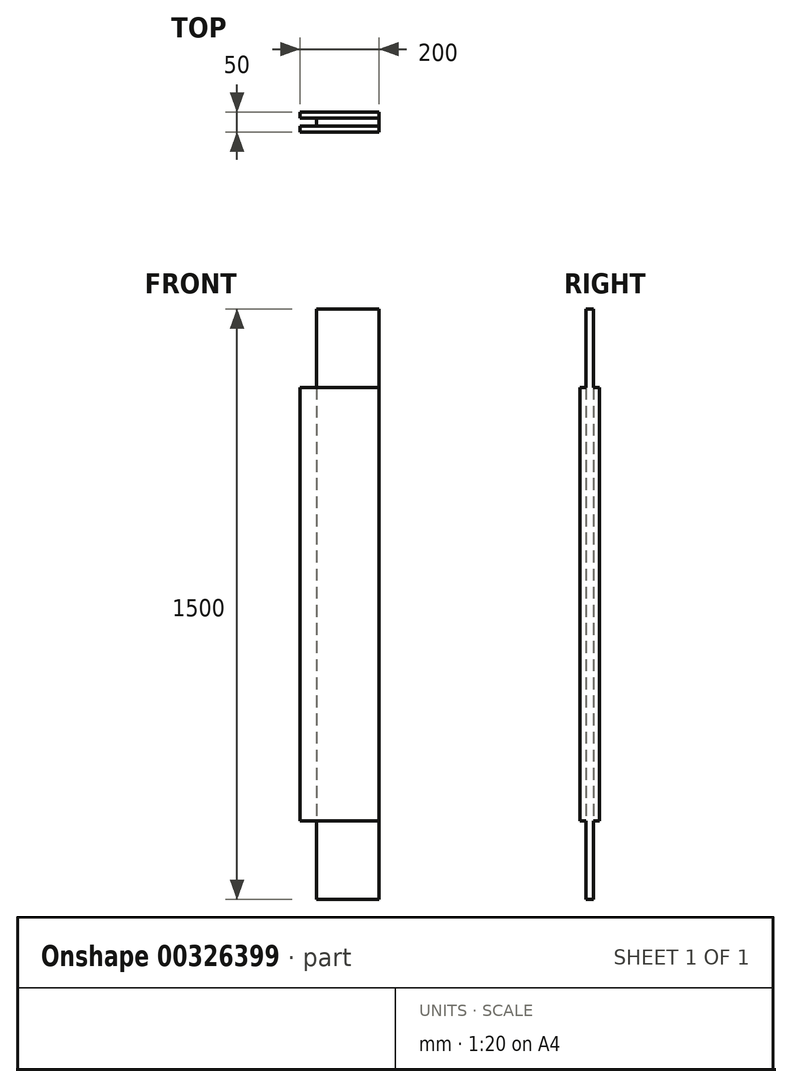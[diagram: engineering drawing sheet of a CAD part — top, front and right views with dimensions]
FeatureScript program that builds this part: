
annotation { "Feature Type Name" : "Feature", "Feature Type Description" : "" }
export const myFeature = defineFeature(function(context is Context, id is Id, definition is map)
    precondition{}
    {
        {
            var Q0;
            Q0=qCreatedBy(makeId("Top.planeOp"),FACE);
            var sketch = newSketch(context, id + "F0", { "sketchPlane" : qUnion([Q0])});
            skLineSegment(sketch, "E0.bottom", {"start": v(0, 0) * mm, "end": v(0, 0) * mm});
            skLineSegment(sketch, "E0.top", {"start": v(0, -16.02) * mm, "end": v(0, -16.02) * mm});
            skLineSegment(sketch, "E0.left", {"start": v(0, 0) * mm, "end": v(0, -16.02) * mm});
            skLineSegment(sketch, "E0.right", {"start": v(0, 0) * mm, "end": v(0, -16.02) * mm});
            skPoint(sketch, "E0.middle", {"position": v(0, -8) * mm});
            skLineSegment(sketch, "E1.bottom", {"start": v(-100, 25) * mm, "end": v(100, 25) * mm});
            skLineSegment(sketch, "E1.top", {"start": v(-100, -25) * mm, "end": v(100, -25) * mm});
            skLineSegment(sketch, "E1.left", {"start": v(-100, 25) * mm, "end": v(-100, -25) * mm});
            skLineSegment(sketch, "E1.right", {"start": v(100, 25) * mm, "end": v(100, -25) * mm});
            skPoint(sketch, "E1.middle", {"position": v(0, 0) * mm});
            skSolve(sketch);
        }
        {
            var Q0;
            Q0=makeQuery(id+"F0.imprint","IMPRINT",FACE,{"disambiguationData":[TD([[makeQuery(id+"F0.imprint","IMPRINT",EDGE,{"derivedFrom":sQuery(id+"F0.wireOp",EDGE,"E1.bottom")}),-1.0]])]});
            extrude(context, id + "F1", {"entities" : qUnion([Q0]), "endBound" : BoundingType.SYMMETRIC, "depth" : 1500 * mm});
        }
        {
            var Q0;
            Q0=makeQuery(id+"F1.opExtrude","CAP_FACE",FACE,{"disambiguationData":[OSD([sQuery(id+"F0.wireOp",EDGE,"E1.bottom"),sQuery(id+"F0.wireOp",EDGE,"E1.top"),sQuery(id+"F0.wireOp",EDGE,"E1.left"),sQuery(id+"F0.wireOp",EDGE,"E1.right")])],"isStart":true});
            var sketch = newSketch(context, id + "F2", { "sketchPlane" : qUnion([Q0])});
            skLineSegment(sketch, "E2.bottom", {"start": v(100, 25) * mm, "end": v(60, 25) * mm});
            skLineSegment(sketch, "E2.top", {"start": v(100, 10) * mm, "end": v(60, 10) * mm});
            skLineSegment(sketch, "E2.left", {"start": v(100, 25) * mm, "end": v(100, 10) * mm});
            skLineSegment(sketch, "E2.right", {"start": v(60, 25) * mm, "end": v(60, 10) * mm});
            skLineSegment(sketch, "E3.MirrorCS", {"start": v(60, -25) * mm, "end": v(60, -10) * mm});
            skLineSegment(sketch, "E4.MirrorCS", {"start": v(100, -25) * mm, "end": v(100, -10) * mm});
            skLineSegment(sketch, "E5.MirrorCS", {"start": v(100, -25) * mm, "end": v(60, -25) * mm});
            skLineSegment(sketch, "E6.MirrorCS", {"start": v(100, -10) * mm, "end": v(60, -10) * mm});
            skLineSegment(sketch, "E7.bottom", {"start": v(-100, -10) * mm, "end": v(-58, -10) * mm});
            skLineSegment(sketch, "E7.top", {"start": v(-100, 10) * mm, "end": v(-58, 10) * mm});
            skLineSegment(sketch, "E7.left", {"start": v(-100, -10) * mm, "end": v(-100, 10) * mm});
            skLineSegment(sketch, "E7.right", {"start": v(-58, -10) * mm, "end": v(-58, 10) * mm});
            skSolve(sketch);
        }
        {
            var Q0;
            Q0=makeQuery(id+"F2.imprint","IMPRINT",FACE,{"disambiguationData":[TD([[makeQuery(id+"F2.imprint","IMPRINT",EDGE,{"derivedFrom":sQuery(id+"F2.wireOp",EDGE,"E7.bottom")}),1.0]])]});
            var Q1;
            Q1=makeQuery(id+"F1.opExtrude","CAP_FACE",FACE,{"disambiguationData":[OSD([sQuery(id+"F0.wireOp",EDGE,"E1.bottom"),sQuery(id+"F0.wireOp",EDGE,"E1.top"),sQuery(id+"F0.wireOp",EDGE,"E1.left"),sQuery(id+"F0.wireOp",EDGE,"E1.right")])],"isStart":true});
            extrude(context, id + "F3", {"entities" : qUnion([Q0]), "operationType" : NewBodyOperationType.REMOVE, "endBound" : BoundingType.UP_TO_NEXT, "oppositeDirection" : true, "endBoundEntityFace" : qUnion([Q1]), "depth" : 25 * mm});
        }
        {
            var Q0;
            {var subQ1=sQuery(id+"F0.wireOp",EDGE,"E1.left");var subQ2=sQuery(id+"F0.wireOp",EDGE,"E1.top");Q0=makeQuery(id+"F3.boolean.opBoolean","SPLIT",FACE,{"disambiguationData":[TD([makeQuery(id+"F1.opExtrude","SWEPT_FACE",FACE,{"disambiguationData":[OSD([subQ2])]})])],"derivedFrom":makeQuery(id+"F1.opExtrude","SWEPT_FACE",FACE,{"disambiguationData":[OSD([subQ1])]})});}
            var sketch = newSketch(context, id + "F4", { "sketchPlane" : qUnion([Q0])});
            skLineSegment(sketch, "E8.bottom", {"start": v(25, -750) * mm, "end": v(10, -750) * mm});
            skLineSegment(sketch, "E8.top", {"start": v(25, -550) * mm, "end": v(10, -550) * mm});
            skLineSegment(sketch, "E8.left", {"start": v(25, -750) * mm, "end": v(25, -550) * mm});
            skLineSegment(sketch, "E8.right", {"start": v(10, -750) * mm, "end": v(10, -550) * mm});
            skLineSegment(sketch, "E9.MirrorCS", {"start": v(25, 750) * mm, "end": v(10, 750) * mm});
            skLineSegment(sketch, "E10.MirrorCS", {"start": v(25, 550) * mm, "end": v(10, 550) * mm});
            skLineSegment(sketch, "E11.MirrorCS", {"start": v(10, 750) * mm, "end": v(10, 550) * mm});
            skLineSegment(sketch, "E12.MirrorCS", {"start": v(25, 750) * mm, "end": v(25, 550) * mm});
            skLineSegment(sketch, "E13.MirrorCS", {"start": v(-25, -750) * mm, "end": v(-10, -750) * mm});
            skLineSegment(sketch, "E14.MirrorCS", {"start": v(-25, -550) * mm, "end": v(-10, -550) * mm});
            skLineSegment(sketch, "E15.MirrorCS", {"start": v(-25, -750) * mm, "end": v(-25, -550) * mm});
            skLineSegment(sketch, "E16.MirrorCS", {"start": v(-10, -750) * mm, "end": v(-10, -550) * mm});
            skLineSegment(sketch, "E17.MirrorCS", {"start": v(-25, 550) * mm, "end": v(-10, 550) * mm});
            skLineSegment(sketch, "E18.MirrorCS", {"start": v(-25, 750) * mm, "end": v(-10, 750) * mm});
            skLineSegment(sketch, "E19.MirrorCS", {"start": v(-25, 750) * mm, "end": v(-25, 550) * mm});
            skLineSegment(sketch, "E20.MirrorCS", {"start": v(-10, 750) * mm, "end": v(-10, 550) * mm});
            skSolve(sketch);
        }
        {
            var Q0;
            Q0=makeQuery(id+"F4.imprint","IMPRINT",FACE,{"disambiguationData":[TD([[makeQuery(id+"F4.imprint","IMPRINT",EDGE,{"derivedFrom":sQuery(id+"F4.wireOp",EDGE,"E17.MirrorCS")}),1.0]])]});
            var Q1;
            Q1=makeQuery(id+"F4.imprint","IMPRINT",FACE,{"disambiguationData":[TD([[makeQuery(id+"F4.imprint","IMPRINT",EDGE,{"derivedFrom":sQuery(id+"F4.wireOp",EDGE,"E11.MirrorCS")}),1.0]])]});
            var Q2;
            Q2=makeQuery(id+"F4.imprint","IMPRINT",FACE,{"disambiguationData":[TD([[makeQuery(id+"F4.imprint","IMPRINT",EDGE,{"derivedFrom":sQuery(id+"F4.wireOp",EDGE,"E8.bottom")}),1.0]])]});
            var Q3;
            Q3=makeQuery(id+"F4.imprint","IMPRINT",FACE,{"disambiguationData":[TD([[makeQuery(id+"F4.imprint","IMPRINT",EDGE,{"derivedFrom":sQuery(id+"F4.wireOp",EDGE,"E13.MirrorCS")}),1.0]])]});
            extrude(context, id + "F5", {"entities" : qUnion([Q0, Q1, Q2, Q3]), "operationType" : NewBodyOperationType.REMOVE, "endBound" : BoundingType.UP_TO_NEXT, "oppositeDirection" : true, "depth" : 25 * mm});
        }
    });
